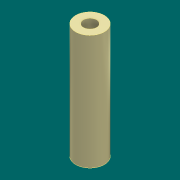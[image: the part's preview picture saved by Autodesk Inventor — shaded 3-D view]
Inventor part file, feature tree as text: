
AUTODESK INVENTOR PART (.ipt)
format: ipt  version: 2016 (Build 200138000, 138)  size: 80,384 bytes
history: native  units: mm
features: extrude x1
ambient origin geometry x8: Origin, YZ Plane, XZ Plane, XY Plane, X Axis, Y Axis, Z Axis, Center Point
bodies: Solid1 (feature_tree)
feature tree (1):
  extrude  "Extrude1"  [1 undecoded]
note: 1 required parameter value undecoded (feature->parameter linkage not recoverable at this tier; creation-order binding heuristic only, values carry confidence <= 0.55)
